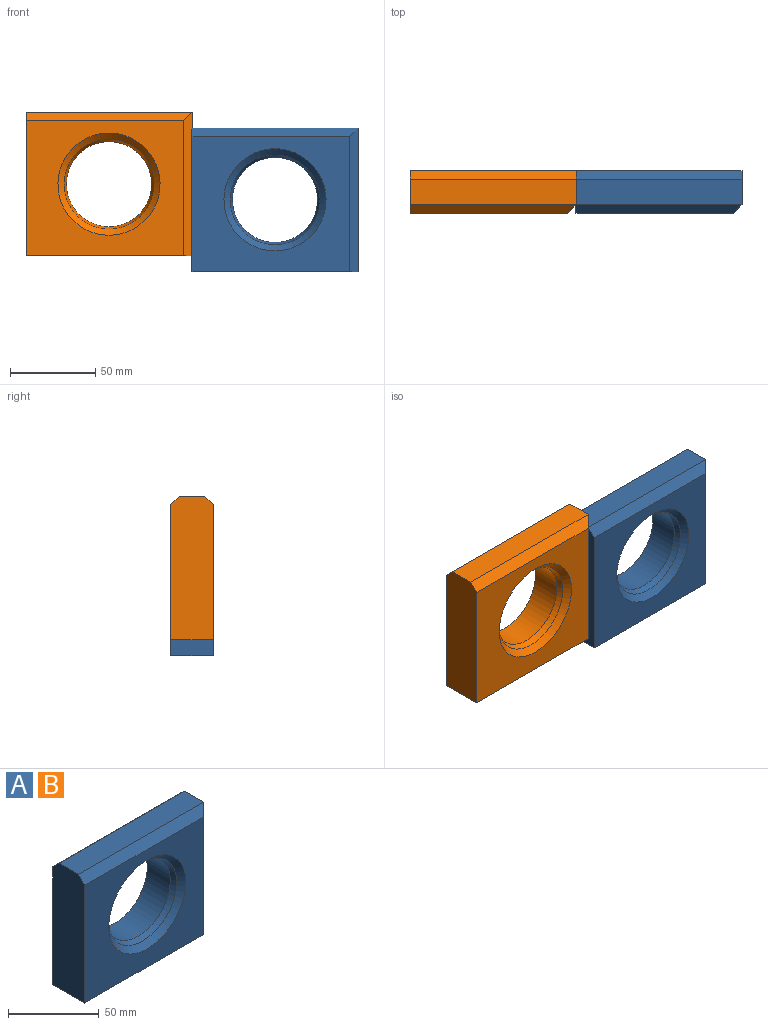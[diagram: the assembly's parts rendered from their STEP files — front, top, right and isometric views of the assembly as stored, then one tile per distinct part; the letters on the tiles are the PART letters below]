
ASSEMBLY  parts=2 mates=1
PART A: 12 faces, bbox 97.5x25x84.3 mm
  f0: plane 97.49x25mm, normal (0,0,-1), area 2424.7mm2, adj f1,f3,f4,f5,f10
  f1: plane 84.29x20mm, normal (1,0,0), area 1673.2mm2, adj f0,f2,f5,f10,f11
  f2: plane 97.49x15mm, normal (0,0,1), area 1462.3mm2, adj f1,f3,f9,f11
  f3: plane 84.29x25mm, normal (-1,0,0), area 2082.2mm2, adj f0,f2,f4,f5,f9,f11
  f4: plane 92.49x79.29mm, normal (0,-1,0), area 4505.4mm2, adj f0,f3,f7,f9,f10
  f5: plane 97.49x79.29mm, normal (0,1,0), area 5765.8mm2, adj f0,f1,f3,f6,f11
  f6: cylinder r=25mm len=50mm, axis (0,-1,0), area 2816.3mm2, adj f5,f8
  f7: cone r=25mm half-angle=45deg, axis (0,-1,0), area 886.9mm2, adj f4,f8
  f8: cone r=25mm half-angle=22.5deg, axis (0,-1,0), area 618.7mm2, adj f6,f7
  f9: plane 97.49x5mm, normal (0,-0.71,0.71), area 671.7mm2, adj f2,f3,f4,f10
  f10: plane 84.29x5mm, normal (0.71,-0.71,0), area 578.3mm2, adj f0,f1,f4,f9
  f11: plane 97.49x5mm, normal (0,0.71,0.71), area 689.3mm2, adj f1,f2,f3,f5
PART B: same geometry as A
PLACE A t=(431.02,95.98,-32.79)mm fixed
PLACE B t=(333.54,95.98,-23.57)mm
MATE planar B.f1 <-> A.f3  axis (1,0,0) through (382.28,85.92,-23.87)mm
